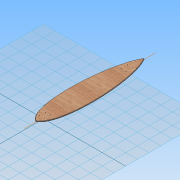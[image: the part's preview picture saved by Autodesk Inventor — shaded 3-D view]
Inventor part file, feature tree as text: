
AUTODESK INVENTOR PART (.ipt)
format: ipt  version: 2014 (Build 180170000, 170)  size: 200,704 bytes
history: native  units: in
note: dims shown in document units (in); Inventor stores cm internally (conversion verified against a paired STEP export)
features: fillet x2, sketch x1, extrude x1, hole x1, other x1, reference x1
ambient origin geometry x8: Origin, YZ Plane, XZ Plane, XY Plane, X Axis, Y Axis, Z Axis, Center Point
bodies: Solid1 (feature_tree)
feature tree (7):
  sketch  "Sketch1"  dims[d0=0.375in d1=0.0in d2=0.125in d3=0.125in d4=1.0in d5=1.0in d6=0.201in d7=0.75in d8=0.375in d9=0.25in d10=0.5635in d11=1.0in d12=0.8108in d13=2.125in d14=0.8125in d15=2.125in]
  extrude  "Extrusion1"  Depth=0.125in
  hole  "Hole1"  [1 undecoded]
  fillet  "Fillet1"  Radius=2.125in
  fillet  "Fillet2"  Radius=0.8125in
  other  "Work Axis1"
  reference  "Reference1"
note: 1 required parameter value undecoded (feature->parameter linkage not recoverable at this tier; creation-order binding heuristic only, values carry confidence <= 0.55)
